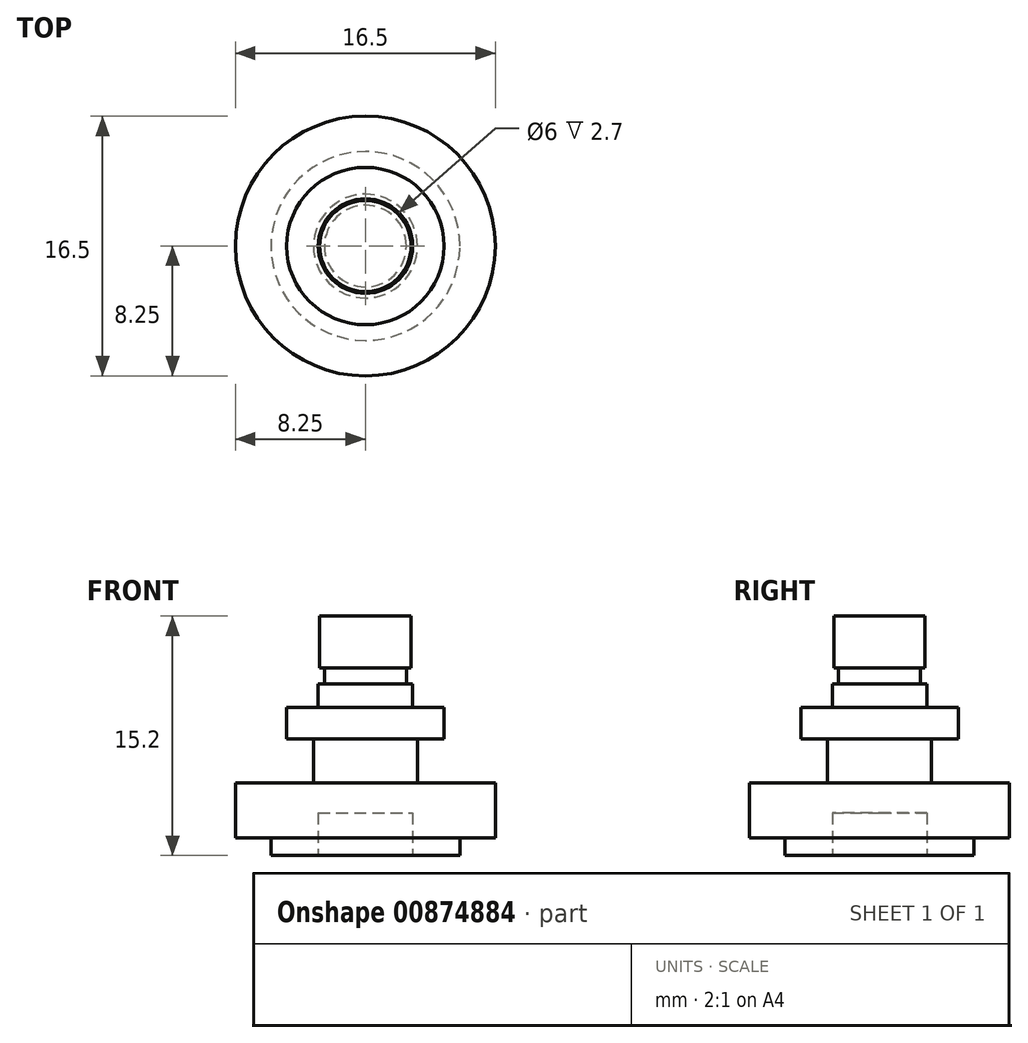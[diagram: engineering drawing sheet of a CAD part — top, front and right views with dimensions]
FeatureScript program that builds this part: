
annotation { "Feature Type Name" : "Feature", "Feature Type Description" : "" }
export const myFeature = defineFeature(function(context is Context, id is Id, definition is map)
    precondition{}
    {
        {
            var Q0;
            Q0=qCreatedBy(makeId("Top.planeOp"),FACE);
            var sketch = newSketch(context, id + "F0", { "sketchPlane" : qUnion([Q0])});
            skCircle(sketch, "E0", {"center": v(0, 0) * mm, "radius": 8.25 * mm});
            skCircle(sketch, "E1", {"center": v(0, 0) * mm, "radius": 3.3 * mm});
            skCircle(sketch, "E2", {"center": v(0, 0) * mm, "radius": 6 * mm});
            skSolve(sketch);
        }
        {
            var Q0;
            Q0=makeQuery(id+"F0.imprint","IMPRINT",FACE,{"disambiguationData":[TD([[makeQuery(id+"F0.imprint","IMPRINT",EDGE,{"derivedFrom":sQuery(id+"F0.wireOp",EDGE,"E0")}),1.0]])]});
            var Q1;
            Q1=makeQuery(id+"F0.imprint","IMPRINT",FACE,{"disambiguationData":[TD([[makeQuery(id+"F0.imprint","IMPRINT",EDGE,{"derivedFrom":sQuery(id+"F0.wireOp",EDGE,"E1")}),-1.0]])]});
            extrude(context, id + "F1", {"entities" : qUnion([Q0, Q1]), "depth" : 3.5 * mm, "offsetDistance" : 25 * mm});
        }
        {
            var Q0;
            Q0=makeQuery(id+"F0.imprint","IMPRINT",FACE,{"disambiguationData":[TD([[makeQuery(id+"F0.imprint","IMPRINT",EDGE,{"derivedFrom":sQuery(id+"F0.wireOp",EDGE,"E1")}),1.0]])]});
            extrude(context, id + "F2", {"entities" : qUnion([Q0]), "operationType" : NewBodyOperationType.ADD, "depth" : 6.3 * mm, "offsetDistance" : 25 * mm});
        }
        {
            var Q0;
            Q0=makeQuery(id+"F0.imprint","IMPRINT",FACE,{"disambiguationData":[TD([[makeQuery(id+"F0.imprint","IMPRINT",EDGE,{"derivedFrom":sQuery(id+"F0.wireOp",EDGE,"E1")}),-1.0]])]});
            var Q1;
            Q1=makeQuery(id+"F0.imprint","IMPRINT",FACE,{"disambiguationData":[TD([[makeQuery(id+"F0.imprint","IMPRINT",EDGE,{"derivedFrom":sQuery(id+"F0.wireOp",EDGE,"E1")}),1.0]])]});
            extrude(context, id + "F3", {"entities" : qUnion([Q0, Q1]), "operationType" : NewBodyOperationType.ADD, "oppositeDirection" : true, "depth" : 1.1 * mm, "offsetDistance" : 25 * mm});
        }
        {
            var Q0;
            Q0=makeQuery(id+"F3.opExtrude","CAP_FACE",FACE,{"disambiguationData":[OSD([sQuery(id+"F0.wireOp",EDGE,"E2")])],"isStart":false});
            var sketch = newSketch(context, id + "F4", { "sketchPlane" : qUnion([Q0])});
            skCircle(sketch, "E3", {"center": v(0, 0) * mm, "radius": 3 * mm});
            skSolve(sketch);
        }
        {
            var Q0;
            Q0=makeQuery(id+"F4.imprint","IMPRINT",FACE,{"disambiguationData":[TD([[makeQuery(id+"F4.imprint","IMPRINT",EDGE,{"derivedFrom":sQuery(id+"F4.wireOp",EDGE,"E3")}),1.0]])]});
            extrude(context, id + "F5", {"entities" : qUnion([Q0]), "operationType" : NewBodyOperationType.REMOVE, "oppositeDirection" : true, "depth" : 2.7 * mm, "offsetDistance" : 25 * mm});
        }
        {
            var Q0;
            Q0=makeQuery(id+"F2.opExtrude","CAP_FACE",FACE,{"disambiguationData":[OSD([sQuery(id+"F0.wireOp",EDGE,"E1")])],"isStart":false});
            var sketch = newSketch(context, id + "F6", { "sketchPlane" : qUnion([Q0])});
            skCircle(sketch, "E4", {"center": v(0, 0) * mm, "radius": 5 * mm});
            skCircle(sketch, "E5", {"center": v(0, 0) * mm, "radius": 3 * mm});
            skSolve(sketch);
        }
        {
            var Q0;
            Q0=makeQuery(id+"F6.imprint","IMPRINT",FACE,{"disambiguationData":[TD([[makeQuery(id+"F6.imprint","IMPRINT",EDGE,{"derivedFrom":sQuery(id+"F6.wireOp",EDGE,"E4")}),1.0]])]});
            var Q1;
            Q1=makeQuery(id+"F6.imprint","IMPRINT",FACE,{"disambiguationData":[TD([[makeQuery(id+"F6.imprint","IMPRINT",EDGE,{"derivedFrom":sQuery(id+"F6.wireOp",EDGE,"E5")}),-1.0]])]});
            extrude(context, id + "F7", {"entities" : qUnion([Q0, Q1]), "depth" : 2 * mm, "offsetDistance" : 25 * mm});
        }
        {
            var Q0;
            Q0=makeQuery(id+"F6.imprint","IMPRINT",FACE,{"disambiguationData":[TD([[makeQuery(id+"F6.imprint","IMPRINT",EDGE,{"derivedFrom":sQuery(id+"F6.wireOp",EDGE,"E5")}),1.0]])]});
            extrude(context, id + "F8", {"entities" : qUnion([Q0]), "operationType" : NewBodyOperationType.ADD, "depth" : 3.5 * mm, "offsetDistance" : 25 * mm});
        }
        {
            var Q0;
            Q0=makeQuery(id+"F8.opExtrude","CAP_FACE",FACE,{"disambiguationData":[OSD([sQuery(id+"F6.wireOp",EDGE,"E5")])],"isStart":false});
            var sketch = newSketch(context, id + "F9", { "sketchPlane" : qUnion([Q0])});
            skCircle(sketch, "E6", {"center": v(0, 0) * mm, "radius": 2.6 * mm});
            skSolve(sketch);
        }
        {
            var Q0;
            Q0=makeQuery(id+"F9.imprint","IMPRINT",FACE,{"disambiguationData":[TD([[makeQuery(id+"F9.imprint","IMPRINT",EDGE,{"derivedFrom":sQuery(id+"F9.wireOp",EDGE,"E6")}),1.0]])]});
            extrude(context, id + "F10", {"entities" : qUnion([Q0]), "operationType" : NewBodyOperationType.ADD, "depth" : 1 * mm, "offsetDistance" : 25 * mm});
        }
        {
            var Q0;
            Q0=makeQuery(id+"F10.opExtrude","CAP_FACE",FACE,{"disambiguationData":[OSD([sQuery(id+"F9.wireOp",EDGE,"E6")])],"isStart":false});
            var sketch = newSketch(context, id + "F11", { "sketchPlane" : qUnion([Q0])});
            skCircle(sketch, "E7", {"center": v(0, 0) * mm, "radius": 2.9 * mm});
            skSolve(sketch);
        }
        {
            var Q0;
            Q0 = qSketchRegion(id + "F11", true);
            var Q1;
            Q1 = qConstructionFilter(qBodyType(qCreatedBy(id + "F11" ,EDGE), BodyType.WIRE), ConstructionObject.NO);
            extrude(context, id + "F12", {"entities" : qUnion([Q0]), "operationType" : NewBodyOperationType.ADD, "surfaceEntities" : qUnion([Q1]), "depth" : 3.3 * mm, "offsetDistance" : 25 * mm});
        }
    });
